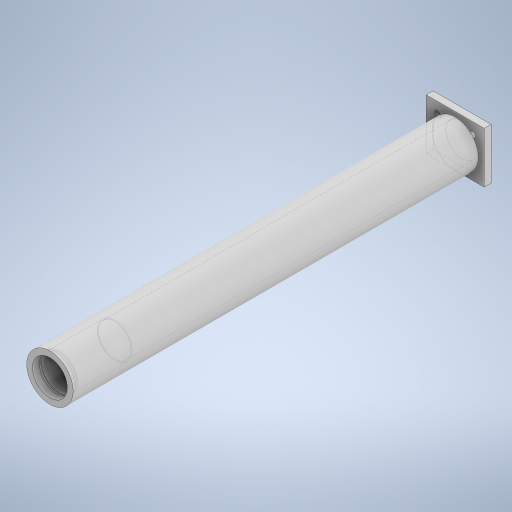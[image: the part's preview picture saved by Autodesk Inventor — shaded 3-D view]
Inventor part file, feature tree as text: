
AUTODESK INVENTOR PART (.ipt)
format: ipt  version: 2023 (Build 270158000, 158)  size: 288,256 bytes
history: native  units: mm
features: extrude x6, sketch x5, projected_geometry x4
ambient origin geometry x8: Origin, YZ Plane, XZ Plane, XY Plane, X Axis, Y Axis, Z Axis, Center Point
bodies: Solid1 (feature_tree)
feature tree (15):
  extrude  "Extrusion1"  Depth=20.0mm
  extrude  "Extrusion2"  Depth=24.0mm
  extrude  "Extrusion3"  Depth=150.0mm
  extrude  "Extrusion4"  Depth=3.0mm TaperAngle=0.0deg
  sketch  "Sketch5"  dims[d12=25.0mm d13=22.0mm d14=15.24mm d15=17.24mm d16=2.54mm d17=3.0mm d18=0.0mm d19=3.0mm d20=0.0mm]
  extrude  "Extrusion5"  Depth=22.0mm
  extrude  "Extrusion6"  Depth=3.0mm
  sketch  "Sketch1"  dims[d0=15.0mm d1=20.0mm]
  sketch  "Sketch2"  dims[d2=24.0mm d3=0.0mm d4=14.0mm]
  projected_geometry  "Projected Loop1"
  sketch  "Sketch3"  dims[d5=150.0mm d6=0.0mm d7=0.5mm]
  projected_geometry  "Projected Loop2"
  sketch  "Sketch4"  dims[d8=1.0mm d9=0.0mm d10=3.0mm d11=0.0mm]
  projected_geometry  "Project Cut Edges1"
  projected_geometry  "Project Cut Edges2"
